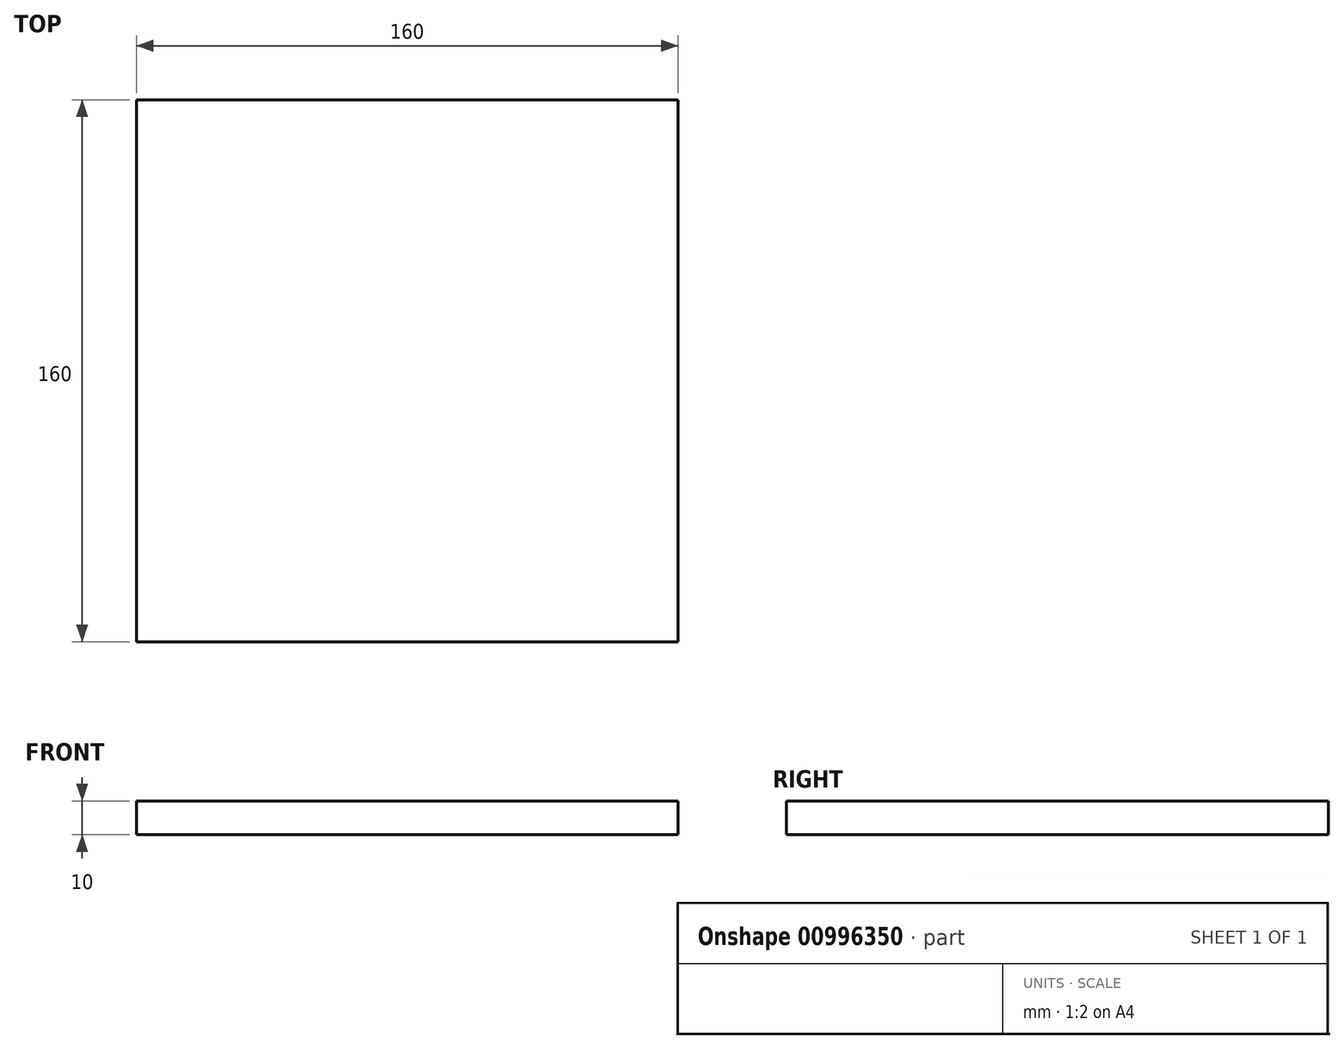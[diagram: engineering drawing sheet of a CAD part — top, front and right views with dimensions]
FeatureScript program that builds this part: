
annotation { "Feature Type Name" : "Feature", "Feature Type Description" : "" }
export const myFeature = defineFeature(function(context is Context, id is Id, definition is map)
    precondition{}
    {
        {
            var Q0;
            Q0=qCreatedBy(makeId("Top.planeOp"),FACE);
            var sketch = newSketch(context, id + "F0", { "sketchPlane" : qUnion([Q0])});
            skLineSegment(sketch, "E0.bottom", {"start": v(-70.92, 98.76) * mm, "end": v(89.08, 98.76) * mm});
            skLineSegment(sketch, "E0.top", {"start": v(-70.92, -61.24) * mm, "end": v(89.08, -61.24) * mm});
            skLineSegment(sketch, "E0.left", {"start": v(-70.92, 98.76) * mm, "end": v(-70.92, -61.24) * mm});
            skLineSegment(sketch, "E0.right", {"start": v(89.08, 98.76) * mm, "end": v(89.08, -61.24) * mm});
            skSolve(sketch);
        }
        {
            var Q0;
            Q0=makeQuery(id+"F0.imprint","IMPRINT",FACE,{"disambiguationData":[TD([[makeQuery(id+"F0.imprint","IMPRINT",EDGE,{"derivedFrom":sQuery(id+"F0.wireOp",EDGE,"E0.bottom")}),-1.0]])]});
            extrude(context, id + "F1", {"entities" : qUnion([Q0]), "depth" : 10 * mm, "offsetDistance" : 25 * mm});
        }
    });
